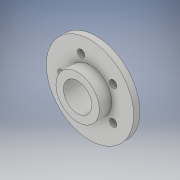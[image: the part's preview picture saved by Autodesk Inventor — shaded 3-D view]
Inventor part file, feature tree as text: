
AUTODESK INVENTOR PART (.ipt)
format: ipt  version: 2017 (Build 210142000, 142)  size: 183,296 bytes
history: native  units: in
note: dims shown in document units (in); Inventor stores cm internally (conversion verified against a paired STEP export)
features: sketch x6, extrude x3, hole x1
ambient origin geometry x8: Origin, YZ Plane, XZ Plane, XY Plane, X Axis, Y Axis, Z Axis, Center Point
bodies: Solid1 (feature_tree)
feature tree (10):
  extrude  "Extrusion1"  Depth=9.4488in TaperAngle=360.0deg
  hole  "Hole1"  [1 undecoded]
  sketch  "Sketch3"  dims[d13=1.9685in d15=360.0deg d17=0.68in]
  sketch  "Sketch4"  dims[d19=0.0in d20=0.3in]
  sketch  "Sketch6"  dims[d21=0.3in d22=0.75in d23=0.375in d24=0.25in d25=0.5635in d26=1.0in d27=0.8108in]
  extrude  "Extrusion4"  Depth=0.68in
  extrude  "Extrusion5"  Depth=0.3in
  sketch  "Sketch1"  dims[d0=3.525in d2=9.4488in d4=360.0deg]
  sketch  "Sketch2"  dims[d6=9.4488in d8=360.0deg d10=0.25in d11=0.0in]
  sketch  "Sketch7"  dims[d36=3.525in d48=1.15in d51=1.75in d52=1.0in d53=0.0in d54=1.0in d55=0.0in d43=1.0in d44=1.0in]
note: 1 required parameter value undecoded (feature->parameter linkage not recoverable at this tier; creation-order binding heuristic only, values carry confidence <= 0.55)
